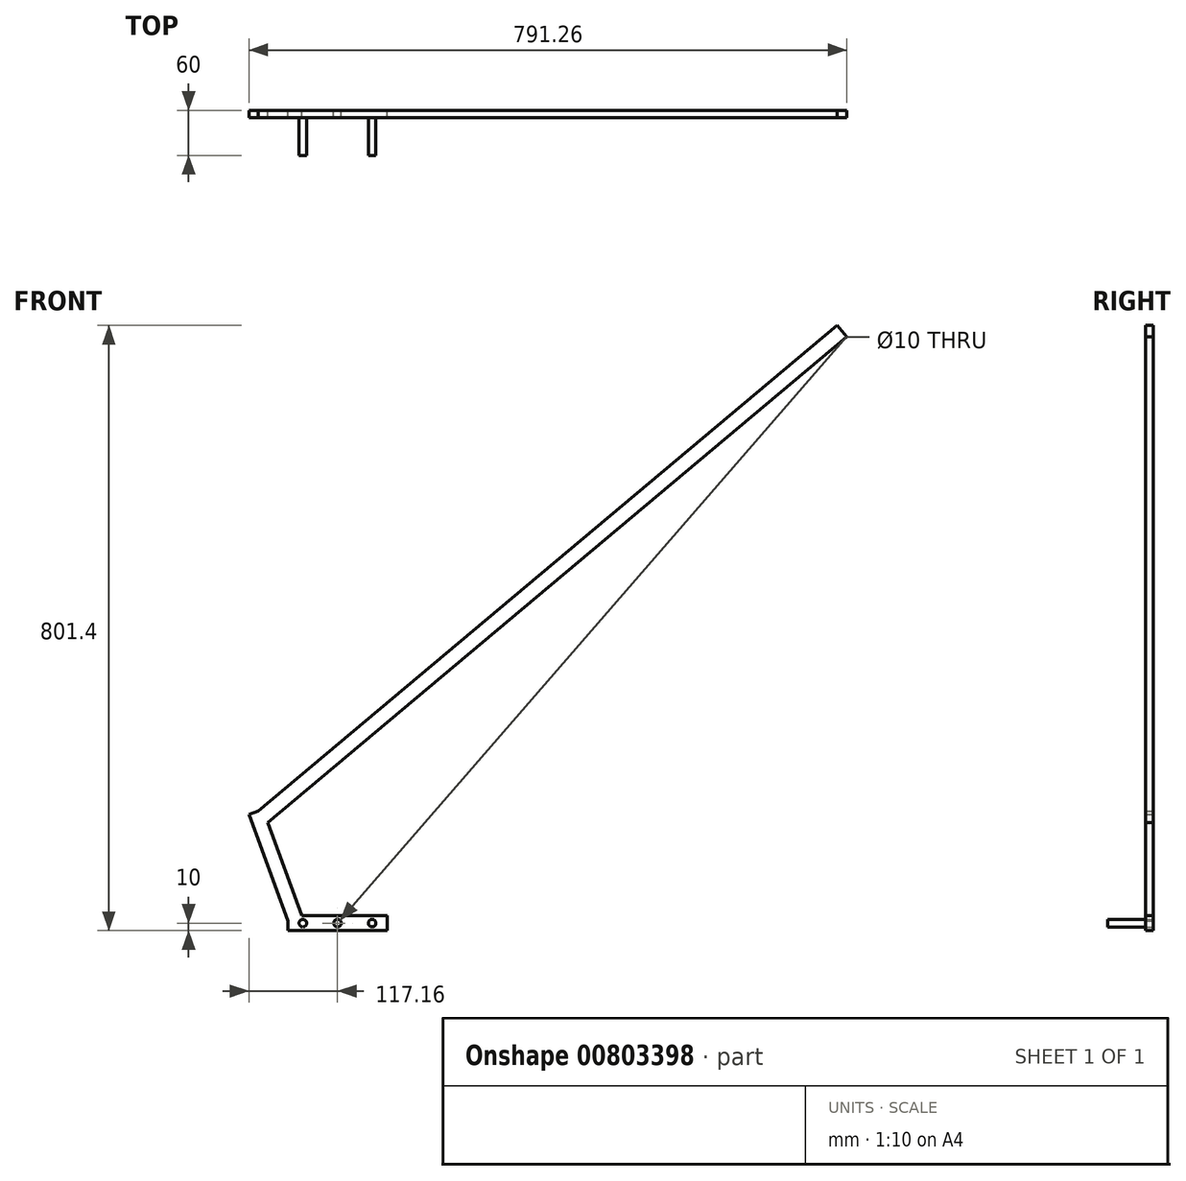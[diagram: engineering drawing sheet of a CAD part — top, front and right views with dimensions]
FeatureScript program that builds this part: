
annotation { "Feature Type Name" : "Feature", "Feature Type Description" : "" }
export const myFeature = defineFeature(function(context is Context, id is Id, definition is map)
    precondition{}
    {
        {
            var Q0;
            Q0=qCreatedBy(makeId("Front.planeOp"),FACE);
            var sketch = newSketch(context, id + "F0", { "sketchPlane" : qUnion([Q0])});
            skLineSegment(sketch, "E0.bottom", {"start": v(-65.86, -10) * mm, "end": v(65.86, -10) * mm});
            skLineSegment(sketch, "E0.top", {"start": v(-65.86, 10) * mm, "end": v(65.86, 10) * mm});
            skLineSegment(sketch, "E0.left", {"start": v(-65.86, -10) * mm, "end": v(-65.86, 10) * mm});
            skLineSegment(sketch, "E0.right", {"start": v(65.86, -10) * mm, "end": v(65.86, 10) * mm});
            skPoint(sketch, "E0.middle", {"position": v(0, 0) * mm});
            skLineSegment(sketch, "E1", {"start": v(-65.86, 0) * mm, "end": v(65.86, 0) * mm, "construction": true});
            skCircle(sketch, "E2", {"center": v(0, 0) * mm, "radius": 5 * mm});
            skSolve(sketch);
        }
        {
            var Q0;
            Q0=makeQuery(id+"F0.imprint","IMPRINT",FACE,{"disambiguationData":[TD([[makeQuery(id+"F0.imprint","IMPRINT",EDGE,{"derivedFrom":sQuery(id+"F0.wireOp",EDGE,"E0.bottom")}),1.0]])]});
            extrude(context, id + "F1", {"entities" : qUnion([Q0]), "depth" : 10 * mm, "offsetDistance" : 25 * mm});
        }
        {
            var Q0;
            Q0=makeQuery(id+"F1.opExtrude","CAP_FACE",FACE,{"disambiguationData":[OSD([sQuery(id+"F0.wireOp",EDGE,"E0.bottom"),sQuery(id+"F0.wireOp",EDGE,"E0.top"),sQuery(id+"F0.wireOp",EDGE,"E0.left"),sQuery(id+"F0.wireOp",EDGE,"E0.right"),sQuery(id+"F0.wireOp",EDGE,"E2")])],"isStart":false});
            var sketch = newSketch(context, id + "F2", { "sketchPlane" : qUnion([Q0])});
            skCircle(sketch, "E3", {"center": v(-45.86, 0) * mm, "radius": 5 * mm});
            skCircle(sketch, "E4", {"center": v(45.86, 0) * mm, "radius": 5 * mm});
            skSolve(sketch);
        }
        {
            var Q0;
            Q0=makeQuery(id+"F2.imprint","IMPRINT",FACE,{"disambiguationData":[TD([[makeQuery(id+"F2.imprint","IMPRINT",EDGE,{"derivedFrom":sQuery(id+"F2.wireOp",EDGE,"E3")}),1.0]])]});
            var Q1;
            Q1=makeQuery(id+"F2.imprint","IMPRINT",FACE,{"disambiguationData":[TD([[makeQuery(id+"F2.imprint","IMPRINT",EDGE,{"derivedFrom":sQuery(id+"F2.wireOp",EDGE,"E4")}),1.0]])]});
            extrude(context, id + "F3", {"entities" : qUnion([Q0, Q1]), "operationType" : NewBodyOperationType.ADD, "depth" : 50 * mm, "offsetDistance" : 25 * mm});
        }
        {
            var Q0;
            Q0=qCreatedBy(makeId("Front.planeOp"),FACE);
            var sketch = newSketch(context, id + "F4", { "sketchPlane" : qUnion([Q0])});
            skLineSegment(sketch, "E5", {"start": v(-65.86, 3.16) * mm, "end": v(-117.16, 144.11) * mm});
            skLineSegment(sketch, "E6", {"start": v(-117.16, 144.11) * mm, "end": v(-98.37, 150.95) * mm});
            skLineSegment(sketch, "E7", {"start": v(-98.37, 150.95) * mm, "end": v(-47.06, 10) * mm});
            skLineSegment(sketch, "E8", {"start": v(-65.86, 3.16) * mm, "end": v(-47.06, 10) * mm});
            skSolve(sketch);
        }
        {
            var Q0;
            Q0=makeQuery(id+"F4.imprint","IMPRINT",FACE,{"disambiguationData":[TD([[makeQuery(id+"F4.imprint","IMPRINT",EDGE,{"derivedFrom":sQuery(id+"F4.wireOp",EDGE,"E5")}),-1.0]])]});
            extrude(context, id + "F5", {"entities" : qUnion([Q0]), "operationType" : NewBodyOperationType.ADD, "depth" : 10 * mm, "offsetDistance" : 25 * mm});
        }
        {
            var Q0;
            Q0=qCreatedBy(makeId("Front.planeOp"),FACE);
            var sketch = newSketch(context, id + "F6", { "sketchPlane" : qUnion([Q0])});
            skLineSegment(sketch, "E9", {"start": v(-104.8, 148.61) * mm, "end": v(661.25, 791.4) * mm});
            skLineSegment(sketch, "E10", {"start": v(661.25, 791.4) * mm, "end": v(674.1, 776.08) * mm});
            skLineSegment(sketch, "E11", {"start": v(674.1, 776.08) * mm, "end": v(-91.94, 133.3) * mm});
            skLineSegment(sketch, "E12", {"start": v(-104.8, 148.61) * mm, "end": v(-91.94, 133.3) * mm});
            skSolve(sketch);
        }
        {
            var Q0;
            Q0=makeQuery(id+"F6.imprint","IMPRINT",FACE,{"disambiguationData":[TD([[makeQuery(id+"F6.imprint","IMPRINT",EDGE,{"derivedFrom":sQuery(id+"F6.wireOp",EDGE,"E9")}),-1.0]])]});
            extrude(context, id + "F7", {"entities" : qUnion([Q0]), "operationType" : NewBodyOperationType.ADD, "depth" : 10 * mm, "offsetDistance" : 25 * mm});
        }
    });
